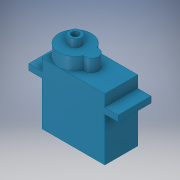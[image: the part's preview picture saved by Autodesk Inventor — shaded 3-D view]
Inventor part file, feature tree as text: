
AUTODESK INVENTOR PART (.ipt)
format: ipt  version: 2017 (Build 210142000, 142)  size: 158,208 bytes
history: native  units: in
note: dims shown in document units (in); Inventor stores cm internally (conversion verified against a paired STEP export)
features: extrude x5, sketch x5, projected_geometry x1
ambient origin geometry x8: Origin, YZ Plane, XZ Plane, XY Plane, X Axis, Y Axis, Z Axis, Center Point
bodies: Solid1 (feature_tree)
feature tree (11):
  extrude  "Extrusion1"  Depth=0.885in
  extrude  "Extrusion2"  Depth=0.087in
  extrude  "Extrusion3"  Depth=0.192in TaperAngle=0.0deg
  extrude  "Extrusion4"  Depth=0.136in
  extrude  "Extrusion5"  Depth=0.182in
  sketch  "Sketch1"  dims[d0=0.897in d1=0.885in]
  sketch  "Sketch2"  dims[d2=0.472in d3=0.0in d4=0.087in]
  projected_geometry  "Projected Loop1"
  sketch  "Sketch3"  dims[d5=0.169in d6=0.192in d7=0.0in]
  sketch  "Sketch4"  dims[d8=1.089in d9=0.0in d10=0.136in]
  sketch  "Sketch5"  dims[d11=0.043in d12=0.182in d13=0.168in d15=0.1in d16=0.0in d17=0.2in d18=0.182in d19=0.0in d20=0.178in d21=0.101in d22=0.112in d23=0.0in]
